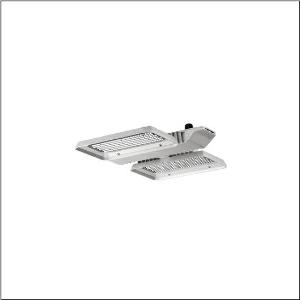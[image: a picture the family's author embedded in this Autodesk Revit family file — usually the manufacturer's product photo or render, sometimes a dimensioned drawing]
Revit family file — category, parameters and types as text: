
# Revit family: highbay_11_51hl62d14dca
name_source: partatom
category: Lighting Fixtures
units: mm (PartAtom-declared; Revit-internal decimal feet)

## family parameters
Cut with Voids When Loaded = No
Host = Face
Light Source = No
Part Type = Normal
Room Calculation Point = No
Round Connector Dimension = Use Diameter
Shared = No

## types (1)
- --- (1 x LED, 10020 lm, 55.6 W, 4000K)
    Apparent Load = 56 VA
    CIE Flux Codes = 89 96 99 100 100
    Color Rendering = 80
    Color Temperature = 4000K
    Default Elevation = 1800 mm
    Description = Highbay 11, LED high bay luminaire, primary light control with lens, of PMMA, light emission: direct distribution, primary light characteristic: symmetric, installation type: surface-mounted, suspended mounting, for 1x 2x LED, rated luminous flux: 10.020lm, luminous efficacy: 180lm/W, light colour: 840, colour temperature: 4000K, control gear: ECG DALI, with terminal, 5-pole, max. 2.5mm², mains connection: 230..240V, AC, 50/60Hz, rated input power: 56W, LED unit, of diecast aluminium, coated, metallic grey (RAL 9006), length: 470mm, width: 500mm, height: 65mm, housing, of diecast aluminium, coated, metallic grey (RAL 9006), protection rating (complete): IP65, insulation class (complete): insulation class I (protective earthing), certification: CE, ENEC, VDE, UKCA, protection symbol: D, impact resistance: IK08 with glass or PC cover, permissible operating ambient temperature: -35..+70°C, corresponds to IFS (International Featured Standards) requirements for safety and quality in the food industry, reducing of maximum allowable ambient temperature of 5°C with ceiling mounting, packaging unit: 1 piece
    Height = 95 mm
    Lamp = 1 x LED
    Lamp Light Flux = 10020 lm
    Lamp Power = 55.6 W
    Lamp count = 1
    Length = 468 mm
    Luminous efficacy = 180 lm/W
    Manufacturer = Siteco
    ModVariant = No
    Model = 51HL62D14DCA
    Mounting Place = Ceiling
    Mounting Type = Pendant
    Number of Poles = 1
    OnlyDefault = Yes
    Power Factor = 1
    Product Name = Highbay 11
    Product group = LED high bay luminaire
    ProductGroupID = 903
    Protection Class = Protection class I
    Protection Degree = IP 65
    RLX_Detail_Level = 1
    RLX_Emergency_Light_Flux = 0 lm
    RLX_Emergency_Type = 0
    RLX_Emergency_Type_DB = No
    RlxData = <blob elided: 70753 chars, md5=27ed8e14>
    Socket = socket
    Standby Power = 0 W
    System Light Flux = 10020 lm
    System Power = 56 W
    Type Comments = factory setting: luminous flux: 100 % | dim-lin: 254 | 315 mA
    Type Image = l_1003425.jpg
    URL = http://relux.com
    VarID = @adj_145889
    Voltage = 0 V
    Weight = 0.00 kg
    Width = 501 mm

## geometry (parser evidence)
native form markers: Blend x4, Sweep x13
no freeform markers — native parametric forms only
